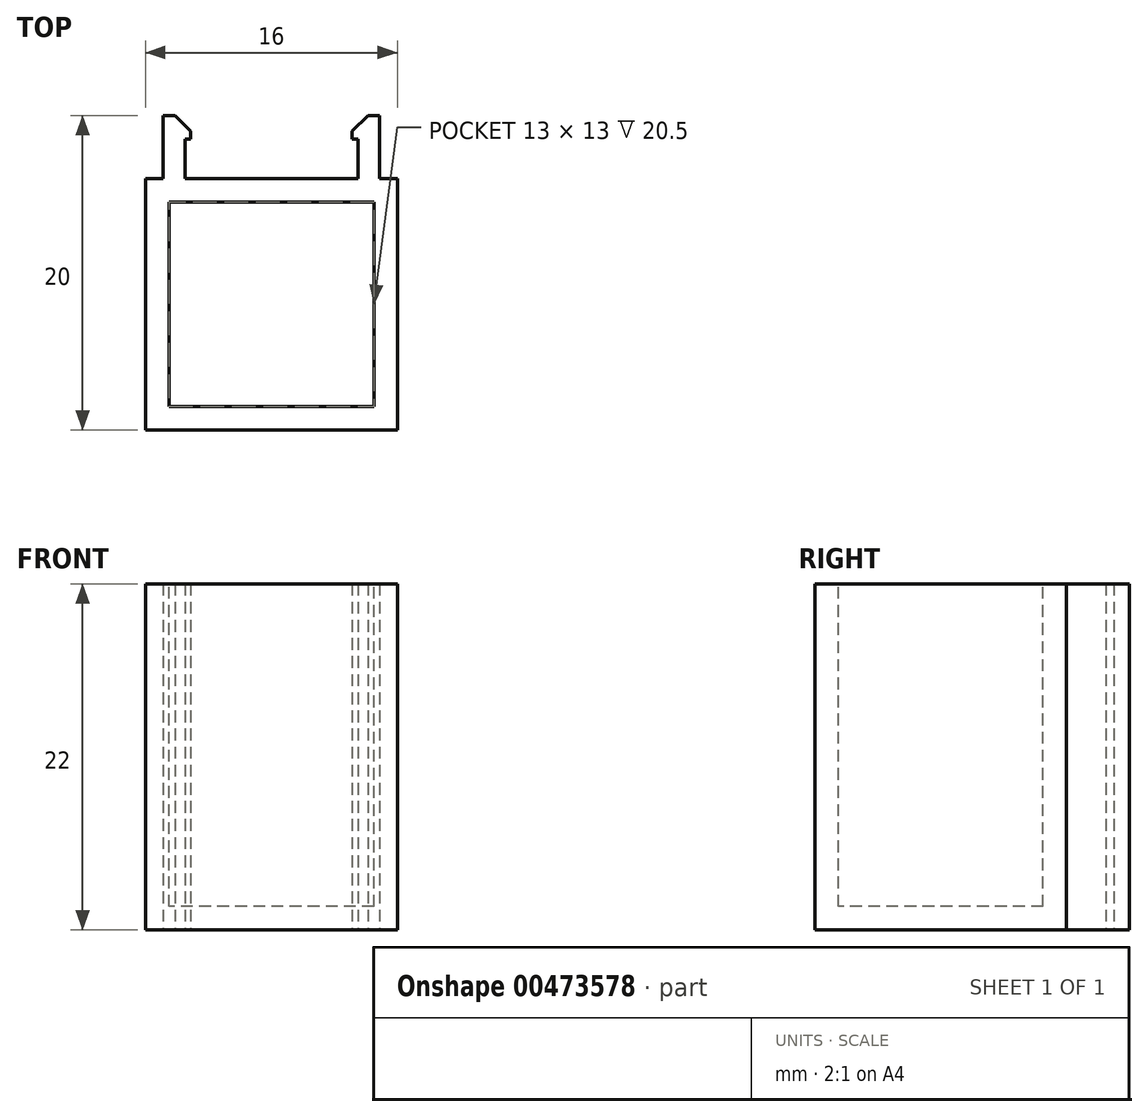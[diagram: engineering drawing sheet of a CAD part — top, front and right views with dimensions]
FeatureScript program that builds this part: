
annotation { "Feature Type Name" : "Feature", "Feature Type Description" : "" }
export const myFeature = defineFeature(function(context is Context, id is Id, definition is map)
    precondition{}
    {
        {
            var Q0;
            Q0=qCreatedBy(makeId("Top.planeOp"),FACE);
            var sketch = newSketch(context, id + "F0", { "sketchPlane" : qUnion([Q0])});
            skLineSegment(sketch, "E0.bottom", {"start": v(8, 8) * mm, "end": v(-8, 8) * mm});
            skLineSegment(sketch, "E0.top", {"start": v(8, -8) * mm, "end": v(-8, -8) * mm});
            skLineSegment(sketch, "E0.left", {"start": v(8, 8) * mm, "end": v(8, -8) * mm});
            skLineSegment(sketch, "E0.right", {"start": v(-8, 8) * mm, "end": v(-8, -8) * mm});
            skPoint(sketch, "E0.middle", {"position": v(0, 0) * mm});
            skLineSegment(sketch, "E1.bottom", {"start": v(6.87, 12) * mm, "end": v(6.12, 12) * mm});
            skLineSegment(sketch, "E1.left", {"start": v(6.87, 12) * mm, "end": v(6.88, -8) * mm});
            skLineSegment(sketch, "E1.right", {"start": v(-6.88, 12) * mm, "end": v(-6.87, -8) * mm});
            skLineSegment(sketch, "E2.left", {"start": v(5.13, 11) * mm, "end": v(5.13, -8) * mm});
            skLineSegment(sketch, "E2.right", {"start": v(-5.12, 11) * mm, "end": v(-5.12, -8) * mm});
            skLineSegment(sketch, "E3.trimOffspring", {"start": v(-6.12, 12) * mm, "end": v(-6.88, 12) * mm});
            skPoint(sketch, "E1.top.end.orphan", {"position": v(5.13, -12) * mm});
            skPoint(sketch, "E1.top.start.orphan", {"position": v(6.88, -12) * mm});
            skPoint(sketch, "E4.trimOffspring.start.orphan", {"position": v(-5.12, -12) * mm});
            skPoint(sketch, "E5.orphan", {"position": v(-6.87, -12) * mm});
            skPoint(sketch, "E6.visualSharp", {"position": v(-5.12, 12) * mm});
            skArc(sketch, "E6.filletArc", {"start": v(-5.12, 11) * mm, "mid": v(-5.42, 11.7) * mm, "end": v(-6.12, 12) * mm});
            skPoint(sketch, "E7.visualSharp", {"position": v(5.13, 12) * mm});
            skArc(sketch, "E7.filletArc", {"start": v(6.12, 12) * mm, "mid": v(5.42, 11.7) * mm, "end": v(5.13, 11) * mm});
            skLineSegment(sketch, "E8", {"start": v(-6.12, 12) * mm, "end": v(-5.12, 11) * mm});
            skLineSegment(sketch, "E9", {"start": v(6.12, 12) * mm, "end": v(5.13, 11) * mm});
            skLineSegment(sketch, "E10.bottom", {"start": v(5.5, 10.5) * mm, "end": v(-5.5, 10.5) * mm});
            skLineSegment(sketch, "E10.top", {"start": v(5.5, -10.5) * mm, "end": v(-5.5, -10.5) * mm});
            skLineSegment(sketch, "E10.left", {"start": v(5.5, 10.5) * mm, "end": v(5.5, -10.5) * mm});
            skLineSegment(sketch, "E10.right", {"start": v(-5.5, 10.5) * mm, "end": v(-5.5, -10.5) * mm});
            skSolve(sketch);
        }
        {
            var Q0;
            {var subQ0=sQuery(id+"F0.wireOp",EDGE,"E2.left");var subQ1=sQuery(id+"F0.wireOp",EDGE,"E0.bottom");var subQ2=makeQuery(id+"F0.imprint","INTERSECT",VERTEX,{"derivedFrom":[subQ1,subQ0]});Q0=makeQuery(id+"F0.imprint","IMPRINT",FACE,{"disambiguationData":[TD([[makeQuery(id+"F0.imprint","IMPRINT",EDGE,{"disambiguationData":[TD([[subQ2,-1.0]])],"derivedFrom":subQ1}),1.0]])]});}
            var Q1;
            {var subQ0=sQuery(id+"F0.wireOp",EDGE,"E1.right");var subQ1=sQuery(id+"F0.wireOp",EDGE,"E0.bottom");var subQ2=makeQuery(id+"F0.imprint","INTERSECT",VERTEX,{"derivedFrom":[subQ1,subQ0]});Q1=makeQuery(id+"F0.imprint","IMPRINT",FACE,{"disambiguationData":[TD([[makeQuery(id+"F0.imprint","IMPRINT",EDGE,{"disambiguationData":[TD([[subQ2,1.0]])],"derivedFrom":subQ1}),1.0]])]});}
            var Q2;
            {var subQ0=sQuery(id+"F0.wireOp",EDGE,"E0.right");Q2=makeQuery(id+"F0.imprint","IMPRINT",FACE,{"disambiguationData":[TD([[makeQuery(id+"F0.imprint","IMPRINT",EDGE,{"derivedFrom":subQ0}),1.0]])]});}
            var Q3;
            {var subQ0=sQuery(id+"F0.wireOp",EDGE,"E1.left");var subQ1=sQuery(id+"F0.wireOp",EDGE,"E0.bottom");var subQ2=makeQuery(id+"F0.imprint","INTERSECT",VERTEX,{"derivedFrom":[subQ1,subQ0]});Q3=makeQuery(id+"F0.imprint","IMPRINT",FACE,{"disambiguationData":[TD([[makeQuery(id+"F0.imprint","IMPRINT",EDGE,{"disambiguationData":[TD([[subQ2,-1.0]])],"derivedFrom":subQ1}),1.0]])]});}
            var Q4;
            {var subQ0=sQuery(id+"F0.wireOp",EDGE,"E0.left");Q4=makeQuery(id+"F0.imprint","IMPRINT",FACE,{"disambiguationData":[TD([[makeQuery(id+"F0.imprint","IMPRINT",EDGE,{"derivedFrom":subQ0}),-1.0]])]});}
            var Q5;
            {var subQ0=sQuery(id+"F0.wireOp",EDGE,"E1.right");var subQ1=sQuery(id+"F0.wireOp",EDGE,"E0.bottom");var subQ2=makeQuery(id+"F0.imprint","INTERSECT",VERTEX,{"derivedFrom":[subQ1,subQ0]});Q5=makeQuery(id+"F0.imprint","IMPRINT",FACE,{"disambiguationData":[TD([[makeQuery(id+"F0.imprint","IMPRINT",EDGE,{"disambiguationData":[TD([[subQ2,1.0]])],"derivedFrom":subQ1}),-1.0]])]});}
            var Q6;
            {var subQ0=sQuery(id+"F0.wireOp",EDGE,"E1.left");var subQ1=sQuery(id+"F0.wireOp",EDGE,"E0.bottom");var subQ2=makeQuery(id+"F0.imprint","INTERSECT",VERTEX,{"derivedFrom":[subQ1,subQ0]});Q6=makeQuery(id+"F0.imprint","IMPRINT",FACE,{"disambiguationData":[TD([[makeQuery(id+"F0.imprint","IMPRINT",EDGE,{"disambiguationData":[TD([[subQ2,-1.0]])],"derivedFrom":subQ1}),-1.0]])]});}
            var Q7;
            {var subQ0=sQuery(id+"F0.wireOp",EDGE,"E2.right");var subQ1=sQuery(id+"F0.wireOp",EDGE,"E0.bottom");var subQ2=makeQuery(id+"F0.imprint","INTERSECT",VERTEX,{"derivedFrom":[subQ1,subQ0]});Q7=makeQuery(id+"F0.imprint","IMPRINT",FACE,{"disambiguationData":[TD([[makeQuery(id+"F0.imprint","IMPRINT",EDGE,{"disambiguationData":[TD([[subQ2,-1.0]])],"derivedFrom":subQ1}),1.0]])]});}
            var Q8;
            {var subQ0=sQuery(id+"F0.wireOp",EDGE,"E10.left");var subQ1=sQuery(id+"F0.wireOp",EDGE,"E0.bottom");var subQ2=makeQuery(id+"F0.imprint","INTERSECT",VERTEX,{"derivedFrom":[subQ1,subQ0]});Q8=makeQuery(id+"F0.imprint","IMPRINT",FACE,{"disambiguationData":[TD([[makeQuery(id+"F0.imprint","IMPRINT",EDGE,{"disambiguationData":[TD([[subQ2,-1.0]])],"derivedFrom":subQ1}),1.0]])]});}
            extrude(context, id + "F1", {"entities" : qUnion([Q0, Q1, Q2, Q3, Q4, Q5, Q6, Q7, Q8]), "depth" : 22 * mm});
        }
        {
            var Q0;
            Q0=makeQuery(id+"F1.opExtrude","CAP_FACE",FACE,{"disambiguationData":[OSD([sQuery(id+"F0.wireOp",EDGE,"E0.bottom"),sQuery(id+"F0.wireOp",EDGE,"E0.top"),sQuery(id+"F0.wireOp",EDGE,"E0.left"),sQuery(id+"F0.wireOp",EDGE,"E0.right"),sQuery(id+"F0.wireOp",EDGE,"E1.bottom"),sQuery(id+"F0.wireOp",EDGE,"E1.left"),sQuery(id+"F0.wireOp",EDGE,"E1.right"),sQuery(id+"F0.wireOp",EDGE,"E2.left"),sQuery(id+"F0.wireOp",EDGE,"E2.right"),sQuery(id+"F0.wireOp",EDGE,"E3.trimOffspring"),sQuery(id+"F0.wireOp",EDGE,"E8"),sQuery(id+"F0.wireOp",EDGE,"E9"),sQuery(id+"F0.wireOp",EDGE,"E10.bottom"),sQuery(id+"F0.wireOp",EDGE,"E10.left"),sQuery(id+"F0.wireOp",EDGE,"E10.right")])],"isStart":false});
            var sketch = newSketch(context, id + "F2", { "sketchPlane" : qUnion([Q0])});
            skLineSegment(sketch, "E11.bottom", {"start": v(6.5, 6.5) * mm, "end": v(-6.5, 6.5) * mm});
            skLineSegment(sketch, "E11.top", {"start": v(6.5, -6.5) * mm, "end": v(-6.5, -6.5) * mm});
            skLineSegment(sketch, "E11.left", {"start": v(6.5, 6.5) * mm, "end": v(6.5, -6.5) * mm});
            skLineSegment(sketch, "E11.right", {"start": v(-6.5, 6.5) * mm, "end": v(-6.5, -6.5) * mm});
            skPoint(sketch, "E11.middle", {"position": v(0, 0) * mm});
            skSolve(sketch);
        }
        {
            var Q0;
            Q0=makeQuery(id+"F2.imprint","IMPRINT",FACE,{"disambiguationData":[TD([[makeQuery(id+"F2.imprint","IMPRINT",EDGE,{"derivedFrom":sQuery(id+"F2.wireOp",EDGE,"E11.bottom")}),1.0]])]});
            extrude(context, id + "F3", {"entities" : qUnion([Q0]), "operationType" : NewBodyOperationType.REMOVE, "oppositeDirection" : true, "depth" : 20.5 * mm});
        }
    });
